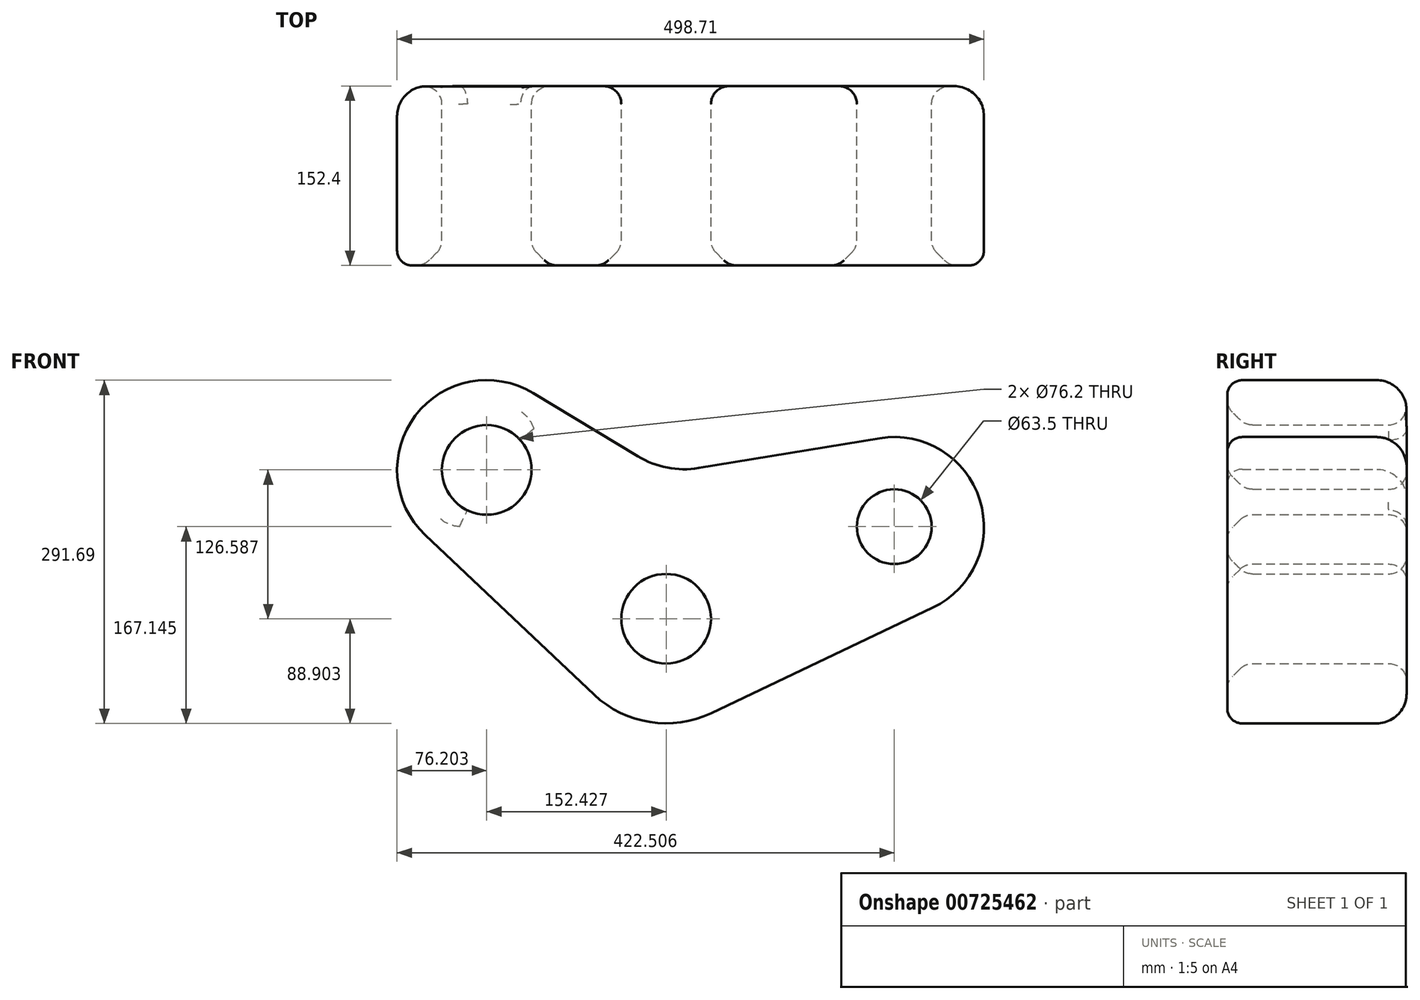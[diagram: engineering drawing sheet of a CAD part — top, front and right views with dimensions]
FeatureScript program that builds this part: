
annotation { "Feature Type Name" : "Feature", "Feature Type Description" : "" }
export const myFeature = defineFeature(function(context is Context, id is Id, definition is map)
    precondition{}
    {
        {
            var Q0;
            Q0=qCreatedBy(makeId("Front.planeOp"),FACE);
            var sketch = newSketch(context, id + "F0", { "sketchPlane" : qUnion([Q0])});
            skCircle(sketch, "E0", {"center": v(0, -27.47) * mm, "radius": 38.1 * mm});
            skCircle(sketch, "E1", {"center": v(0, -27.47) * mm, "radius": 88.9 * mm});
            skCircle(sketch, "E2", {"center": v(-152.43, 99.12) * mm, "radius": 76.2 * mm});
            skCircle(sketch, "E3", {"center": v(193.88, 50.77) * mm, "radius": 76.2 * mm});
            skLineSegment(sketch, "E4", {"start": v(-204.77, 43.74) * mm, "end": v(-61.06, -92.08) * mm});
            skLineSegment(sketch, "E5", {"start": v(-113.02, 164.34) * mm, "end": v(-24.06, 110.6) * mm});
            skLineSegment(sketch, "E6", {"start": v(27.73, 100.63) * mm, "end": v(181.49, 125.96) * mm});
            skLineSegment(sketch, "E7", {"start": v(38.22, -107.73) * mm, "end": v(226.63, -18.03) * mm});
            skPoint(sketch, "E8.visualSharp", {"position": v(0, 96.06) * mm});
            skArc(sketch, "E8.filletArc", {"start": v(-24.06, 110.6) * mm, "mid": v(0.95, 100.99) * mm, "end": v(27.73, 100.63) * mm});
            skCircle(sketch, "E9", {"center": v(-152.43, 99.12) * mm, "radius": 38.1 * mm});
            skCircle(sketch, "E10", {"center": v(193.88, 50.77) * mm, "radius": 31.75 * mm});
            skSolve(sketch);
        }
        {
            var Q0;
            {var subQ3=sQuery(id+"F0.wireOp",EDGE,"E4");Q0=makeQuery(id+"F0.imprint","IMPRINT",FACE,{"disambiguationData":[TD([[makeQuery(id+"F0.imprint","IMPRINT",EDGE,{"derivedFrom":subQ3}),1.0]])]});}
            var Q1;
            Q1=makeQuery(id+"F0.imprint","IMPRINT",FACE,{"disambiguationData":[TD([[makeQuery(id+"F0.imprint","IMPRINT",EDGE,{"derivedFrom":sQuery(id+"F0.wireOp",EDGE,"E9")}),-1.0]])]});
            var Q2;
            Q2=makeQuery(id+"F0.imprint","IMPRINT",FACE,{"disambiguationData":[TD([[makeQuery(id+"F0.imprint","IMPRINT",EDGE,{"derivedFrom":sQuery(id+"F0.wireOp",EDGE,"E0")}),-1.0]])]});
            var Q3;
            Q3=makeQuery(id+"F0.imprint","IMPRINT",FACE,{"disambiguationData":[TD([[makeQuery(id+"F0.imprint","IMPRINT",EDGE,{"derivedFrom":sQuery(id+"F0.wireOp",EDGE,"E10")}),-1.0]])]});
            extrude(context, id + "F1", {"entities" : qUnion([Q0, Q1, Q2, Q3]), "endBound" : BoundingType.SYMMETRIC, "depth" : 152.4 * mm, "offsetDistance" : 25.4 * mm});
        }
        {
            var Q0;
            Q0=makeQuery(id+"F1.opExtrude","CAP_EDGE",EDGE,{"disambiguationData":[OSD([sQuery(id+"F0.wireOp",EDGE,"E9")])],"isStart":false});
            var Q1;
            Q1=makeQuery(id+"F1.opExtrude","CAP_EDGE",EDGE,{"disambiguationData":[OSD([sQuery(id+"F0.wireOp",EDGE,"E0")])],"isStart":false});
            var Q2;
            Q2=makeQuery(id+"F1.opExtrude","CAP_EDGE",EDGE,{"disambiguationData":[OSD([sQuery(id+"F0.wireOp",EDGE,"E10")])],"isStart":false});
            chamfer(context, id + "F2", {"entities" : qUnion([Q0, Q1, Q2]), "width" : 15.24 * mm, "tangentPropagation" : true});
        }
        {
            var Q0;
            Q0=makeQuery(id+"F1.opExtrude","CAP_EDGE",EDGE,{"disambiguationData":[OSD([sQuery(id+"F0.wireOp",EDGE,"E2")])],"isStart":false});
            fillet(context, id + "F3", {"entities" : qUnion([Q0]), "radius" : 12.7 * mm, "tangentPropagation" : true, "allowEdgeOverflow" : false});
        }
        {
            var Q0;
            Q0=makeQuery(id+"F1.opExtrude","CAP_EDGE",EDGE,{"disambiguationData":[OSD([sQuery(id+"F0.wireOp",EDGE,"E6")])],"isStart":true});
            fillet(context, id + "F4", {"entities" : qUnion([Q0]), "radius" : 25.4 * mm, "tangentPropagation" : true, "allowEdgeOverflow" : false});
        }
        {
            var Q0;
            {var subQ0=sQuery(id+"F0.wireOp",EDGE,"E9");Q0=makeQuery(id+"F2.opChamfer","BLEND_EDGE",EDGE,{"blendedFrom":[makeQuery(id+"F1.opExtrude","CAP_EDGE",EDGE,{"disambiguationData":[OSD([subQ0])],"isStart":false}),makeQuery(id+"F1.opExtrude","CAP_FACE",FACE,{"disambiguationData":[OSD([sQuery(id+"F0.wireOp",EDGE,"E0"),sQuery(id+"F0.wireOp",EDGE,"E1"),sQuery(id+"F0.wireOp",EDGE,"E2"),sQuery(id+"F0.wireOp",EDGE,"E3"),sQuery(id+"F0.wireOp",EDGE,"E4"),sQuery(id+"F0.wireOp",EDGE,"E5"),sQuery(id+"F0.wireOp",EDGE,"E6"),sQuery(id+"F0.wireOp",EDGE,"E7"),sQuery(id+"F0.wireOp",EDGE,"E8.filletArc"),subQ0,sQuery(id+"F0.wireOp",EDGE,"E10")])],"isStart":false})],"blendedInto":[makeQuery(id+"F1.opExtrude","CAP_FACE",FACE,{"disambiguationData":[OSD([sQuery(id+"F0.wireOp",EDGE,"E0"),sQuery(id+"F0.wireOp",EDGE,"E1"),sQuery(id+"F0.wireOp",EDGE,"E2"),sQuery(id+"F0.wireOp",EDGE,"E3"),sQuery(id+"F0.wireOp",EDGE,"E4"),sQuery(id+"F0.wireOp",EDGE,"E5"),sQuery(id+"F0.wireOp",EDGE,"E6"),sQuery(id+"F0.wireOp",EDGE,"E7"),sQuery(id+"F0.wireOp",EDGE,"E8.filletArc"),subQ0,sQuery(id+"F0.wireOp",EDGE,"E10")])],"isStart":false})]});}
            var Q1;
            {var subQ0=sQuery(id+"F0.wireOp",EDGE,"E9");Q1=makeQuery(id+"F2.opChamfer","BLEND_EDGE",EDGE,{"blendedFrom":[makeQuery(id+"F1.opExtrude","CAP_EDGE",EDGE,{"disambiguationData":[OSD([subQ0])],"isStart":false}),makeQuery(id+"F1.opExtrude","SWEPT_FACE",FACE,{"disambiguationData":[OSD([subQ0])]})],"blendedInto":[makeQuery(id+"F1.opExtrude","SWEPT_FACE",FACE,{"disambiguationData":[OSD([subQ0])]})]});}
            var Q2;
            {var subQ0=sQuery(id+"F0.wireOp",EDGE,"E0");Q2=makeQuery(id+"F2.opChamfer","BLEND_EDGE",EDGE,{"blendedFrom":[makeQuery(id+"F1.opExtrude","CAP_EDGE",EDGE,{"disambiguationData":[OSD([subQ0])],"isStart":false}),makeQuery(id+"F1.opExtrude","CAP_FACE",FACE,{"disambiguationData":[OSD([subQ0,sQuery(id+"F0.wireOp",EDGE,"E1"),sQuery(id+"F0.wireOp",EDGE,"E2"),sQuery(id+"F0.wireOp",EDGE,"E3"),sQuery(id+"F0.wireOp",EDGE,"E4"),sQuery(id+"F0.wireOp",EDGE,"E5"),sQuery(id+"F0.wireOp",EDGE,"E6"),sQuery(id+"F0.wireOp",EDGE,"E7"),sQuery(id+"F0.wireOp",EDGE,"E8.filletArc"),sQuery(id+"F0.wireOp",EDGE,"E9"),sQuery(id+"F0.wireOp",EDGE,"E10")])],"isStart":false})],"blendedInto":[makeQuery(id+"F1.opExtrude","CAP_FACE",FACE,{"disambiguationData":[OSD([subQ0,sQuery(id+"F0.wireOp",EDGE,"E1"),sQuery(id+"F0.wireOp",EDGE,"E2"),sQuery(id+"F0.wireOp",EDGE,"E3"),sQuery(id+"F0.wireOp",EDGE,"E4"),sQuery(id+"F0.wireOp",EDGE,"E5"),sQuery(id+"F0.wireOp",EDGE,"E6"),sQuery(id+"F0.wireOp",EDGE,"E7"),sQuery(id+"F0.wireOp",EDGE,"E8.filletArc"),sQuery(id+"F0.wireOp",EDGE,"E9"),sQuery(id+"F0.wireOp",EDGE,"E10")])],"isStart":false})]});}
            var Q3;
            {var subQ0=sQuery(id+"F0.wireOp",EDGE,"E0");Q3=makeQuery(id+"F2.opChamfer","BLEND_EDGE",EDGE,{"blendedFrom":[makeQuery(id+"F1.opExtrude","CAP_EDGE",EDGE,{"disambiguationData":[OSD([subQ0])],"isStart":false}),makeQuery(id+"F1.opExtrude","SWEPT_FACE",FACE,{"disambiguationData":[OSD([subQ0])]})],"blendedInto":[makeQuery(id+"F1.opExtrude","SWEPT_FACE",FACE,{"disambiguationData":[OSD([subQ0])]})]});}
            var Q4;
            {var subQ0=sQuery(id+"F0.wireOp",EDGE,"E10");Q4=makeQuery(id+"F2.opChamfer","BLEND_EDGE",EDGE,{"blendedFrom":[makeQuery(id+"F1.opExtrude","CAP_EDGE",EDGE,{"disambiguationData":[OSD([subQ0])],"isStart":false}),makeQuery(id+"F1.opExtrude","SWEPT_FACE",FACE,{"disambiguationData":[OSD([subQ0])]})],"blendedInto":[makeQuery(id+"F1.opExtrude","SWEPT_FACE",FACE,{"disambiguationData":[OSD([subQ0])]})]});}
            var Q5;
            {var subQ0=sQuery(id+"F0.wireOp",EDGE,"E10");Q5=makeQuery(id+"F2.opChamfer","BLEND_EDGE",EDGE,{"blendedFrom":[makeQuery(id+"F1.opExtrude","CAP_EDGE",EDGE,{"disambiguationData":[OSD([subQ0])],"isStart":false}),makeQuery(id+"F1.opExtrude","CAP_FACE",FACE,{"disambiguationData":[OSD([sQuery(id+"F0.wireOp",EDGE,"E0"),sQuery(id+"F0.wireOp",EDGE,"E1"),sQuery(id+"F0.wireOp",EDGE,"E2"),sQuery(id+"F0.wireOp",EDGE,"E3"),sQuery(id+"F0.wireOp",EDGE,"E4"),sQuery(id+"F0.wireOp",EDGE,"E5"),sQuery(id+"F0.wireOp",EDGE,"E6"),sQuery(id+"F0.wireOp",EDGE,"E7"),sQuery(id+"F0.wireOp",EDGE,"E8.filletArc"),sQuery(id+"F0.wireOp",EDGE,"E9"),subQ0])],"isStart":false})],"blendedInto":[makeQuery(id+"F1.opExtrude","CAP_FACE",FACE,{"disambiguationData":[OSD([sQuery(id+"F0.wireOp",EDGE,"E0"),sQuery(id+"F0.wireOp",EDGE,"E1"),sQuery(id+"F0.wireOp",EDGE,"E2"),sQuery(id+"F0.wireOp",EDGE,"E3"),sQuery(id+"F0.wireOp",EDGE,"E4"),sQuery(id+"F0.wireOp",EDGE,"E5"),sQuery(id+"F0.wireOp",EDGE,"E6"),sQuery(id+"F0.wireOp",EDGE,"E7"),sQuery(id+"F0.wireOp",EDGE,"E8.filletArc"),sQuery(id+"F0.wireOp",EDGE,"E9"),subQ0])],"isStart":false})]});}
            var Q6;
            Q6=makeQuery(id+"F1.opExtrude","CAP_EDGE",EDGE,{"disambiguationData":[OSD([sQuery(id+"F0.wireOp",EDGE,"E10")])],"isStart":true});
            var Q7;
            Q7=makeQuery(id+"F1.opExtrude","CAP_EDGE",EDGE,{"disambiguationData":[OSD([sQuery(id+"F0.wireOp",EDGE,"E0")])],"isStart":true});
            var Q8;
            Q8=makeQuery(id+"F1.opExtrude","CAP_EDGE",EDGE,{"disambiguationData":[OSD([sQuery(id+"F0.wireOp",EDGE,"E9")])],"isStart":true});
            fillet(context, id + "F5", {"entities" : qUnion([Q0, Q1, Q2, Q3, Q4, Q5, Q6, Q7, Q8]), "radius" : 15.24 * mm, "tangentPropagation" : true, "allowEdgeOverflow" : false});
        }
    });
